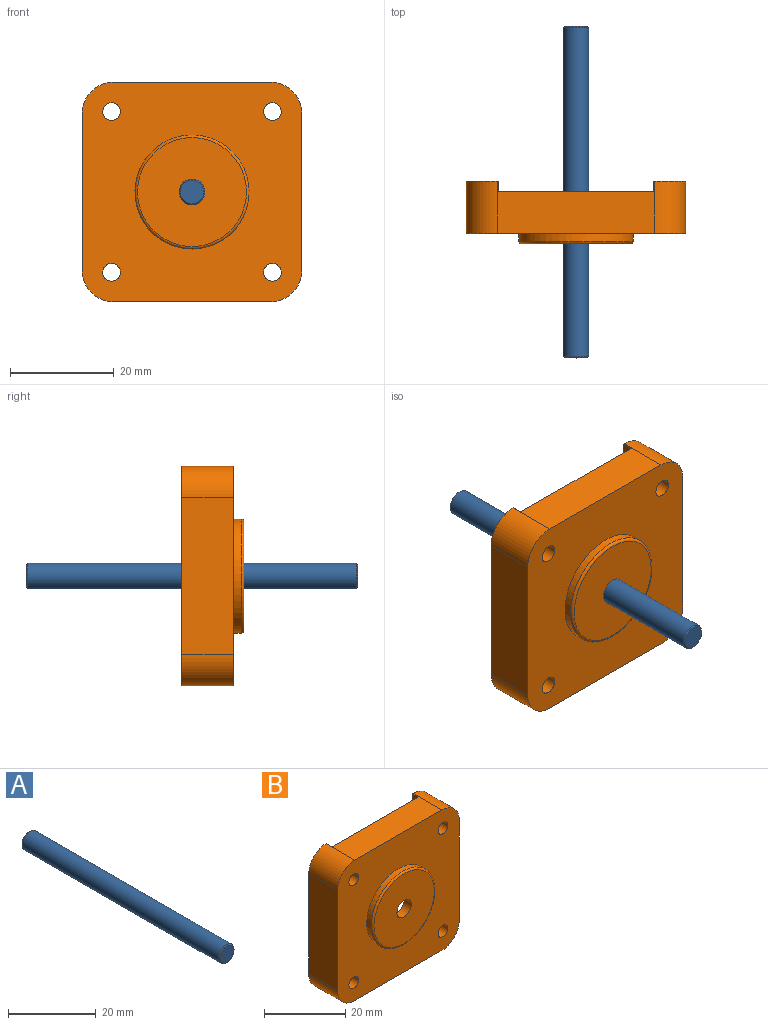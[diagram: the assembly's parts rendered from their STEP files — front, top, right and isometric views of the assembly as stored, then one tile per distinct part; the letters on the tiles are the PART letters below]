
ASSEMBLY  parts=2 mates=2
PART A: 5 faces, bbox 5x64x5 mm
  f0: cylinder r=2.5mm len=63.5mm, axis (0,1,0), area 997.5mm2, adj f3,f4
  f1: plane 4.5x4.5mm, normal (0,-1,0), area 15.9mm2, adj f4
  f2: plane 4.5x4.5mm, normal (0,1,0), area 15.9mm2, adj f3
  f3: cone r=2.5mm half-angle=45deg, axis (0,-1,0), area 5.3mm2, adj f0,f2
  f4: cone r=2.25mm half-angle=45deg, axis (0,1,0), area 5.3mm2, adj f0,f1
PART B: 36 faces, bbox 42.3x12x42.3 mm
  f0: plane 42.3x6.15mm, normal (0,1,0), area 113.8mm2, adj f1,f6,f7,f8,f12,f13,f17,f21
  f1: plane 2.5x2mm, normal (-1,0,0), area 5mm2, adj f0,f2,f12,f27
  f2: plane 30x2.5mm, normal (0,1,0), area 75mm2, adj f1,f3,f12,f27
  f3: plane 2.5x2mm, normal (1,0,0), area 5mm2, adj f2,f4,f12,f27
  f4: plane 42.3x6.15mm, normal (0,1,0), area 113.8mm2, adj f3,f8,f9,f10,f11,f12,f15,f23
  f5: cylinder r=2.5mm len=5mm, axis (0,-1,0), area 39.3mm2, adj f19,f31
  f6: plane 30.3x10mm, normal (1,0,0), area 303mm2, adj f0,f7,f13,f14
  f7: cylinder r=6mm len=10mm, axis (0,1,0), area 94.2mm2, adj f0,f6,f8,f14
  f8: plane 30.3x10mm, normal (0,0,1), area 243mm2, adj f0,f4,f7,f9,f14,f15,f16,f17
  f9: cylinder r=6mm len=10mm, axis (0,1,0), area 94.2mm2, adj f4,f8,f10,f14
  f10: plane 30.3x10mm, normal (-1,0,0), area 303mm2, adj f4,f9,f11,f14
  f11: cylinder r=6mm len=10mm, axis (0,1,0), area 94.2mm2, adj f4,f10,f12,f14
  f12: plane 30.3x10mm, normal (0,0,-1), area 243mm2, adj f0,f1,f2,f3,f4,f11,f13,f14
  f13: cylinder r=6mm len=10mm, axis (0,1,0), area 94.2mm2, adj f0,f6,f12,f14
  f14: plane 42.3x42.3mm, normal (0,-1,0), area 1341.9mm2, adj f6,f7,f8,f9,f10,f11,f12,f13
  f15: plane 2.5x2mm, normal (1,0,0), area 5mm2, adj f4,f8,f16,f23
  f16: plane 30x2.5mm, normal (0,1,0), area 75mm2, adj f8,f15,f17,f23
  f17: plane 2.5x2mm, normal (-1,0,0), area 5mm2, adj f0,f8,f16,f23
  f18: cylinder r=11mm len=22mm, axis (0,1,0), area 103.7mm2, adj f14,f20
  f19: plane 21x21mm, normal (0,-1,0), area 326.7mm2, adj f5,f20
  f20: torus R=10.5mm, axis (0,-1,0), area 53.4mm2, adj f18,f19
  f21: plane 30.3x7.5mm, normal (-1,0,0), area 227.2mm2, adj f0,f22,f28,f29
  f22: cylinder r=3.5mm len=7.5mm, axis (0,1,0), area 41.2mm2, adj f0,f21,f23,f29
  f23: plane 30.3x7.5mm, normal (0,0,-1), area 167.3mm2, adj f0,f4,f15,f16,f17,f22,f24,f29
  f24: cylinder r=3.5mm len=7.5mm, axis (0,1,0), area 41.2mm2, adj f4,f23,f25,f29
  f25: plane 30.3x7.5mm, normal (1,0,0), area 227.2mm2, adj f4,f24,f26,f29
  f26: cylinder r=3.5mm len=7.5mm, axis (0,1,0), area 41.2mm2, adj f4,f25,f27,f29
  f27: plane 30.3x7.5mm, normal (0,0,1), area 167.3mm2, adj f0,f1,f2,f3,f4,f26,f28,f29
  f28: cylinder r=3.5mm len=7.5mm, axis (0,1,0), area 41.2mm2, adj f0,f21,f27,f29
  f29: plane 37.3x37.3mm, normal (0,1,0), area 1117.5mm2, adj f21,f22,f23,f24,f25,f26,f27,f28
  f30: cylinder r=8.5mm len=17mm, axis (0,1,0), area 106.8mm2, adj f29,f31
  f31: plane 17x17mm, normal (0,1,0), area 207.3mm2, adj f5,f30
  f32: cylinder r=1.7mm len=3.4mm, axis (0,-1,0), area 26.7mm2, adj f14,f29
  f33: cylinder r=1.7mm len=3.4mm, axis (0,-1,0), area 26.7mm2, adj f14,f29
  f34: cylinder r=1.7mm len=3.4mm, axis (0,-1,0), area 26.7mm2, adj f14,f29
  f35: cylinder r=1.7mm len=3.4mm, axis (0,-1,0), area 26.7mm2, adj f14,f29
PLACE A t=(8.61,13.9,17.87)mm
PLACE B t=(8.61,-16.1,17.87)mm
MATE parallel B.f5 <-> A.f0  axis (0,-1,0) through (8.61,-26.1,17.87)mm
MATE cylindrical A.f0 <-> B.f18  axis (0,1,0) through (8.61,-18.1,17.87)mm
